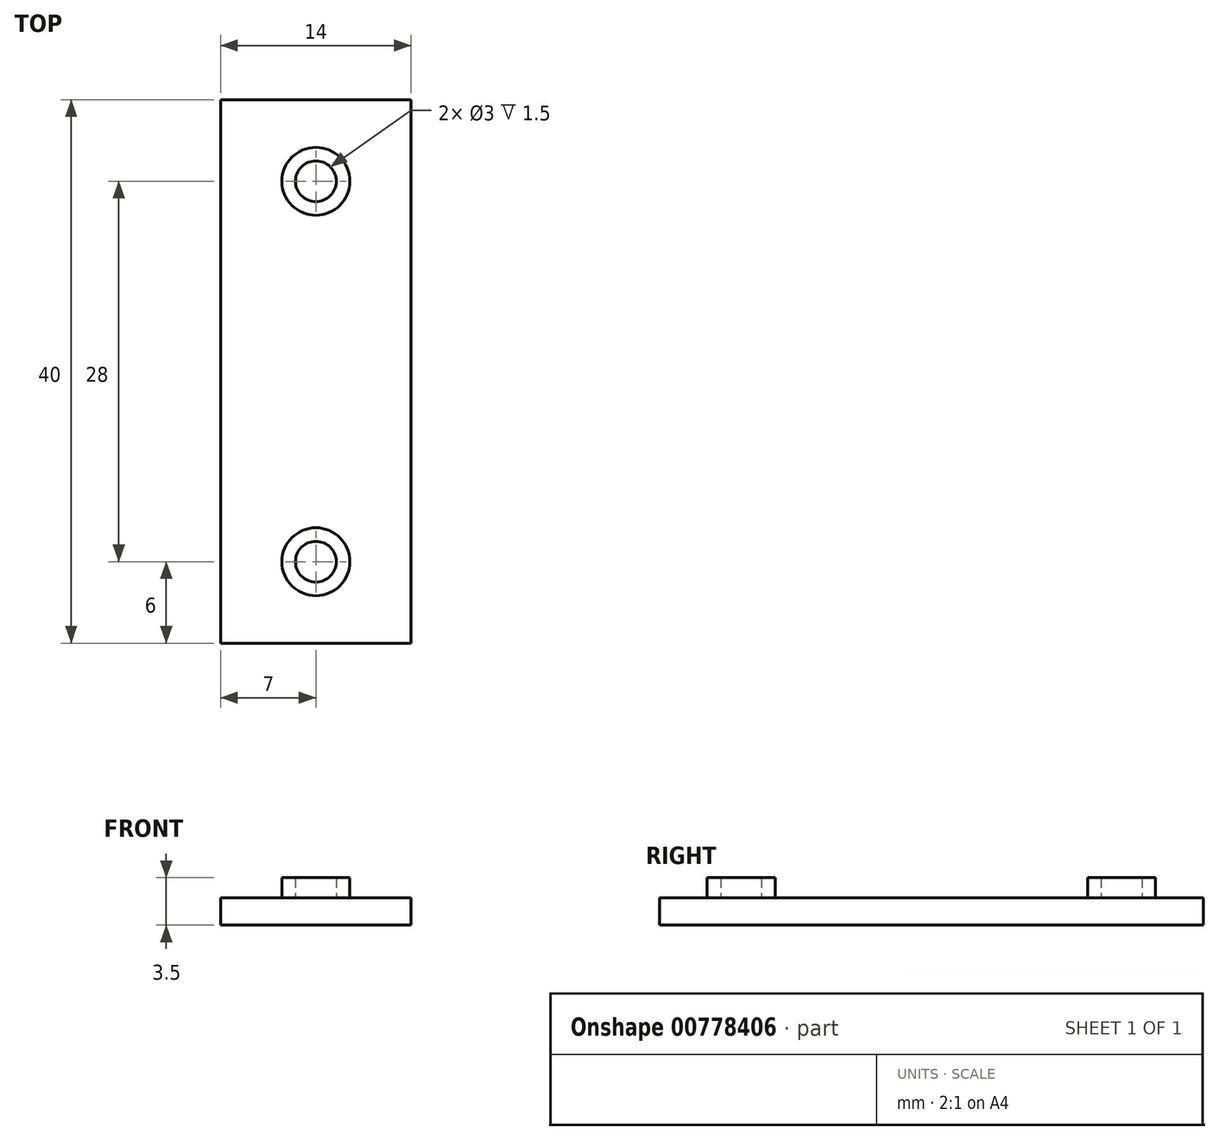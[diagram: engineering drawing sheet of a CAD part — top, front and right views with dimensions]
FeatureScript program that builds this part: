
annotation { "Feature Type Name" : "Feature", "Feature Type Description" : "" }
export const myFeature = defineFeature(function(context is Context, id is Id, definition is map)
    precondition{}
    {
        {
            var Q0;
            Q0=qCreatedBy(makeId("Front.planeOp"),FACE);
            var sketch = newSketch(context, id + "F0", { "sketchPlane" : qUnion([Q0])});
            skLineSegment(sketch, "E0.bottom", {"start": v(7, 0) * mm, "end": v(-7, 0) * mm});
            skLineSegment(sketch, "E0.top", {"start": v(7, 2) * mm, "end": v(-7, 2) * mm});
            skLineSegment(sketch, "E0.left", {"start": v(7, 0) * mm, "end": v(7, 2) * mm});
            skLineSegment(sketch, "E0.right", {"start": v(-7, 0) * mm, "end": v(-7, 2) * mm});
            skPoint(sketch, "E0.middle", {"position": v(0, 1) * mm});
            skSolve(sketch);
        }
        {
            var Q0;
            Q0=makeQuery(id+"F0.imprint","IMPRINT",FACE,{"disambiguationData":[TD([[makeQuery(id+"F0.imprint","IMPRINT",EDGE,{"derivedFrom":sQuery(id+"F0.wireOp",EDGE,"E0.bottom")}),-1.0]])]});
            extrude(context, id + "F1", {"entities" : qUnion([Q0]), "depth" : 20 * mm, "offsetDistance" : 25 * mm, "hasSecondDirection" : true, "secondDirectionOppositeDirection" : true, "secondDirectionDepth" : 20 * mm});
        }
        {
            var Q0;
            Q0=makeQuery(id+"F1.opExtrude","SWEPT_FACE",FACE,{"disambiguationData":[OSD([sQuery(id+"F0.wireOp",EDGE,"E0.top")])]});
            var sketch = newSketch(context, id + "F2", { "sketchPlane" : qUnion([Q0])});
            skLineSegment(sketch, "E1", {"start": v(0, 0) * mm, "end": v(0, -14) * mm, "construction": true});
            skLineSegment(sketch, "E2", {"start": v(0, 0) * mm, "end": v(0, 14) * mm, "construction": true});
            skCircle(sketch, "E3", {"center": v(0, 14) * mm, "radius": 1.5 * mm});
            skCircle(sketch, "E4", {"center": v(0, -14) * mm, "radius": 1.5 * mm});
            skCircle(sketch, "E5", {"center": v(0, 14) * mm, "radius": 2.5 * mm});
            skCircle(sketch, "E6", {"center": v(0, -14) * mm, "radius": 2.5 * mm});
            skSolve(sketch);
        }
        {
            var Q0;
            Q0=makeQuery(id+"F2.imprint","IMPRINT",FACE,{"disambiguationData":[TD([[makeQuery(id+"F2.imprint","IMPRINT",EDGE,{"derivedFrom":sQuery(id+"F2.wireOp",EDGE,"E3")}),-1.0]])]});
            var Q1;
            Q1=makeQuery(id+"F2.imprint","IMPRINT",FACE,{"disambiguationData":[TD([[makeQuery(id+"F2.imprint","IMPRINT",EDGE,{"derivedFrom":sQuery(id+"F2.wireOp",EDGE,"E4")}),-1.0]])]});
            extrude(context, id + "F3", {"entities" : qUnion([Q0, Q1]), "operationType" : NewBodyOperationType.ADD, "depth" : 1.5 * mm, "offsetDistance" : 25 * mm});
        }
    });
